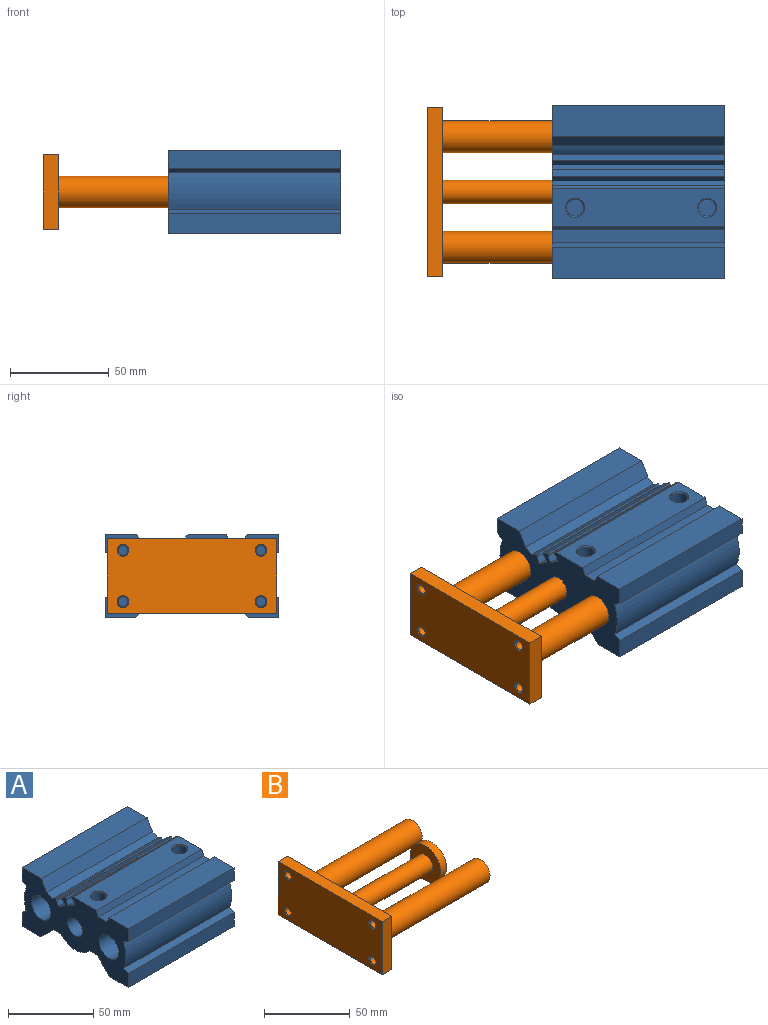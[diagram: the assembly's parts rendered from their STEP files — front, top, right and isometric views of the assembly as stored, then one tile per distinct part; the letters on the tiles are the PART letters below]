
ASSEMBLY  parts=2 mates=1
PART A: 80 faces, bbox 87.5x88x42 mm
  f0: plane 8.57x8.57mm, normal (0,0,1), area 57.6mm2, adj f1
  f1: cylinder r=4.28mm len=8.57mm, axis (0,0,1), area 151.2mm2, adj f0,f79
  f2: plane 87.5x16mm, normal (0,0,1), area 1400mm2, adj f6,f51,f55,f57
  f3: plane 87.5x19.13mm, normal (0,0,1), area 1525mm2, adj f6,f9,f51,f58,f76,f79
  f4: plane 87.5x16mm, normal (0,0,1), area 1400mm2, adj f6,f7,f51,f52
  f5: plane 87.5x15.5mm, normal (0,0,-1), area 1299.7mm2, adj f6,f11,f25,f28,f51,f53
  f6: plane 88x42mm, normal (-1,0,0), area 2432.4mm2, adj f2,f3,f4,f5,f7,f8,f9,f10
  f7: plane 87.5x4mm, normal (0,0.87,0.5), area 404.1mm2, adj f4,f6,f8,f51
  f8: plane 87.5x6.73mm, normal (0,0,1), area 589.3mm2, adj f6,f7,f9,f51
  f9: plane 87.5x4mm, normal (0,-0.94,0.34), area 372.5mm2, adj f3,f6,f8,f51
  f10: plane 87.5x10.5mm, normal (0,-0.71,-0.71), area 1299.3mm2, adj f6,f14,f51,f54
  f11: plane 87.5x10.5mm, normal (0,0.71,-0.71), area 1299.3mm2, adj f5,f6,f12,f51
  f12: plane 87.5x5.93mm, normal (0,0,-1), area 518.6mm2, adj f6,f11,f13,f51
  f13: cylinder r=16mm len=87.5mm, axis (1,0,0), area 2393.9mm2, adj f6,f12,f14,f51
  f14: plane 87.5x5.93mm, normal (0,0,-1), area 518.6mm2, adj f6,f10,f13,f51
  f15: cylinder r=25mm len=87.5mm, axis (1,0,0), area 1668.9mm2, adj f6,f16,f17,f51
  f16: plane 87.5x3.64mm, normal (0,-0.5,0.87), area 367.5mm2, adj f6,f15,f51,f53
  f17: plane 87.5x3.96mm, normal (0,-0.5,-0.87), area 400.5mm2, adj f6,f15,f51,f52
  f18: plane 87.5x3.64mm, normal (0,0.5,0.87), area 367.5mm2, adj f6,f19,f51,f56
  f19: cylinder r=25mm len=87.5mm, axis (1,0,0), area 1668.9mm2, adj f6,f18,f20,f51
  f20: plane 87.5x3.96mm, normal (0,0.5,-0.87), area 400.5mm2, adj f6,f19,f51,f55
  f21: plane 25x25mm, normal (-1,0,0), area 490.9mm2, adj f22
  f22: cylinder r=12.5mm len=55mm, axis (-1,0,0), area 4319.7mm2, adj f21,f23
  f23: plane 25x25mm, normal (1,0,0), area 377.8mm2, adj f22,f24
  f24: cylinder r=6mm len=18.75mm, axis (-1,0,0), area 706.9mm2, adj f6,f23
  f25: cone r=2.46mm half-angle=45deg, axis (0,0,-1), area 13.1mm2, adj f5,f26
  f26: cylinder r=2.46mm len=8.46mm, axis (0,0,1), area 130.7mm2, adj f25,f27
  f27: cone r=882.95mm half-angle=62deg, axis (0,0,-1), area 21.5mm2, adj f26
  f28: cone r=2.46mm half-angle=45deg, axis (0,0,-1), area 13.1mm2, adj f5,f29
  f29: cylinder r=2.46mm len=8.46mm, axis (0,0,1), area 130.7mm2, adj f28,f30
  f30: cone r=882.95mm half-angle=62deg, axis (0,0,-1), area 21.5mm2, adj f29
  f31: cone r=2.46mm half-angle=45deg, axis (0,0,-1), area 13.1mm2, adj f32,f54
  f32: cylinder r=2.46mm len=8.46mm, axis (0,0,1), area 130.7mm2, adj f31,f33
  f33: cone r=882.95mm half-angle=62deg, axis (0,0,-1), area 21.5mm2, adj f32
  f34: cone r=2.46mm half-angle=45deg, axis (0,0,-1), area 13.1mm2, adj f35,f54
  f35: cylinder r=2.46mm len=8.46mm, axis (0,0,1), area 130.7mm2, adj f34,f36
  f36: cone r=882.95mm half-angle=62deg, axis (0,0,-1), area 21.5mm2, adj f35
  f37: cone r=2.46mm half-angle=45deg, axis (1,0,0), area 13.1mm2, adj f38,f51
  f38: cylinder r=2.46mm len=14.46mm, axis (-1,0,0), area 223.3mm2, adj f37,f39
  f39: cone r=882.95mm half-angle=62deg, axis (1,0,0), area 21.5mm2, adj f38
  f40: cone r=2.46mm half-angle=45deg, axis (1,0,0), area 13.1mm2, adj f41,f51
  f41: cylinder r=2.46mm len=14.46mm, axis (-1,0,0), area 223.3mm2, adj f40,f42
  f42: cone r=882.95mm half-angle=62deg, axis (1,0,0), area 21.5mm2, adj f41
  f43: cone r=2.46mm half-angle=45deg, axis (1,0,0), area 13.1mm2, adj f44,f51
  f44: cylinder r=2.46mm len=14.46mm, axis (-1,0,0), area 223.3mm2, adj f43,f45
  f45: cone r=882.95mm half-angle=62deg, axis (1,0,0), area 21.5mm2, adj f44
  f46: cone r=2.46mm half-angle=45deg, axis (1,0,0), area 13.1mm2, adj f47,f51
  f47: cylinder r=2.46mm len=14.46mm, axis (-1,0,0), area 223.3mm2, adj f46,f48
  f48: cone r=882.95mm half-angle=62deg, axis (1,0,0), area 21.5mm2, adj f47
  f49: cylinder r=8mm len=87.5mm, axis (-1,0,0), area 4398.2mm2, adj f6,f51
  f50: cylinder r=8mm len=87.5mm, axis (-1,0,0), area 4398.2mm2, adj f6,f51
  f51: plane 88x42mm, normal (1,0,0), area 2432.4mm2, adj f2,f3,f4,f5,f7,f8,f9,f10
  f52: plane 87.5x9mm, normal (0,-1,0), area 787.5mm2, adj f4,f6,f17,f51
  f53: plane 87.5x10mm, normal (0,-1,0), area 875mm2, adj f5,f6,f16,f51
  f54: plane 87.5x15.5mm, normal (0,0,-1), area 1299.7mm2, adj f6,f10,f31,f34,f51,f56
  f55: plane 87.5x9mm, normal (0,1,0), area 787.5mm2, adj f2,f6,f20,f51
  f56: plane 87.5x10mm, normal (0,1,0), area 875mm2, adj f6,f18,f51,f54
  f57: plane 87.5x7.73mm, normal (0,-0.87,0.5), area 781.1mm2, adj f2,f6,f51,f75
  f58: plane 87.5x1.62mm, normal (0,0.5,0.87), area 163.3mm2, adj f3,f6,f51,f59
  f59: plane 87.5x0.81mm, normal (0,0.87,-0.5), area 82.2mm2, adj f6,f51,f58,f60
  f60: plane 87.5x0.72mm, normal (0,0,-1), area 63.1mm2, adj f6,f51,f59,f61
  f61: plane 87.5x3.2mm, normal (0,0.87,-0.5), area 323.7mm2, adj f6,f51,f60,f62
  f62: plane 87.5x5.46mm, normal (0,0.5,0.87), area 551.2mm2, adj f6,f51,f61,f63
  f63: plane 87.5x3.2mm, normal (0,-0.87,0.5), area 323.7mm2, adj f6,f51,f62,f64
  f64: plane 87.5x0.63mm, normal (0,-0.87,-0.5), area 63.1mm2, adj f6,f51,f63,f65
  f65: plane 87.5x0.81mm, normal (0,-0.87,0.5), area 82.2mm2, adj f6,f51,f64,f66
  f66: plane 87.5x3.77mm, normal (0,0.5,0.87), area 380.6mm2, adj f6,f51,f65,f67
  f67: plane 87.5x0.81mm, normal (0,0.87,-0.5), area 82.2mm2, adj f6,f51,f66,f68
  f68: plane 87.5x0.72mm, normal (0,0,-1), area 63.1mm2, adj f6,f51,f67,f69
  f69: plane 87.5x3.2mm, normal (0,0.87,-0.5), area 323.7mm2, adj f6,f51,f68,f70
  f70: plane 87.5x5.46mm, normal (0,0.5,0.87), area 551.2mm2, adj f6,f51,f69,f71
  f71: plane 87.5x3.2mm, normal (0,-0.87,0.5), area 323.7mm2, adj f6,f51,f70,f72
  f72: plane 87.5x0.63mm, normal (0,-0.87,-0.5), area 63.1mm2, adj f6,f51,f71,f73
  f73: plane 87.5x0.81mm, normal (0,-0.87,0.5), area 82.2mm2, adj f6,f51,f72,f74
  f74: plane 87.5x3.42mm, normal (0,0.5,0.87), area 345.4mm2, adj f6,f51,f73,f75
  f75: cylinder r=14mm len=87.5mm, axis (1,0,0), area 438mm2, adj f6,f51,f57,f74
  f76: cone r=4.86mm half-angle=45deg, axis (0,0,1), area 23.6mm2, adj f3,f77
  f77: cylinder r=4.28mm len=8.57mm, axis (0,0,1), area 151.2mm2, adj f76,f78
  f78: plane 8.57x8.57mm, normal (0,0,1), area 57.6mm2, adj f77
  f79: cone r=4.86mm half-angle=45deg, axis (0,0,1), area 23.6mm2, adj f1,f3
PART B: 26 faces, bbox 96x86x38 mm
  f0: cylinder r=12.5mm len=25mm, axis (-1,0,0), area 392.7mm2, adj f1,f25
  f1: plane 25x25mm, normal (-1,0,0), area 377.8mm2, adj f0,f2
  f2: cylinder r=6mm len=70.75mm, axis (-1,0,0), area 2667.2mm2, adj f1,f3
  f3: plane 86x38mm, normal (1,0,0), area 2639.7mm2, adj f2,f4,f5,f6,f7,f9,f11,f15
  f4: plane 38x8mm, normal (0,1,0), area 304mm2, adj f3,f5,f7,f8
  f5: plane 86x8mm, normal (0,0,1), area 688mm2, adj f3,f4,f6,f8
  f6: plane 38x8mm, normal (0,-1,0), area 304mm2, adj f3,f5,f7,f8
  f7: plane 86x8mm, normal (0,0,-1), area 688mm2, adj f3,f4,f6,f8
  f8: plane 86x38mm, normal (-1,0,0), area 3154.9mm2, adj f4,f5,f6,f7,f13,f16,f19,f22
  f9: cylinder r=8mm len=88mm, axis (-1,0,0), area 4423.4mm2, adj f3,f10
  f10: plane 16x16mm, normal (1,0,0), area 201.1mm2, adj f9
  f11: cylinder r=8mm len=88mm, axis (-1,0,0), area 4423.4mm2, adj f3,f12
  f12: plane 16x16mm, normal (1,0,0), area 201.1mm2, adj f11
  f13: cone r=3mm half-angle=45deg, axis (-1,0,0), area 13.1mm2, adj f8,f14
  f14: cylinder r=2.46mm len=6.92mm, axis (-1,0,0), area 106.8mm2, adj f13,f15
  f15: cone r=2.46mm half-angle=45deg, axis (1,0,0), area 13.1mm2, adj f3,f14
  f16: cone r=3mm half-angle=45deg, axis (-1,0,0), area 13.1mm2, adj f8,f17
  f17: cylinder r=2.46mm len=6.92mm, axis (-1,0,0), area 106.8mm2, adj f16,f18
  f18: cone r=2.46mm half-angle=45deg, axis (1,0,0), area 13.1mm2, adj f3,f17
  f19: cone r=3mm half-angle=45deg, axis (-1,0,0), area 13.1mm2, adj f8,f20
  f20: cylinder r=2.46mm len=6.92mm, axis (-1,0,0), area 106.8mm2, adj f19,f21
  f21: cone r=2.46mm half-angle=45deg, axis (1,0,0), area 13.1mm2, adj f3,f20
  f22: cone r=3mm half-angle=45deg, axis (-1,0,0), area 13.1mm2, adj f8,f23
  f23: cylinder r=2.46mm len=6.92mm, axis (-1,0,0), area 106.8mm2, adj f22,f24
  f24: cone r=2.46mm half-angle=45deg, axis (1,0,0), area 13.1mm2, adj f3,f23
  f25: plane 25x25mm, normal (1,0,0), area 490.9mm2, adj f0
PLACE A t=(32.8,0,0)mm
PLACE B t=(-22.7,0,0)mm
MATE slider B.f11 <-> A.f49  axis (-1,0,0) through (65.3,-28,0)mm
